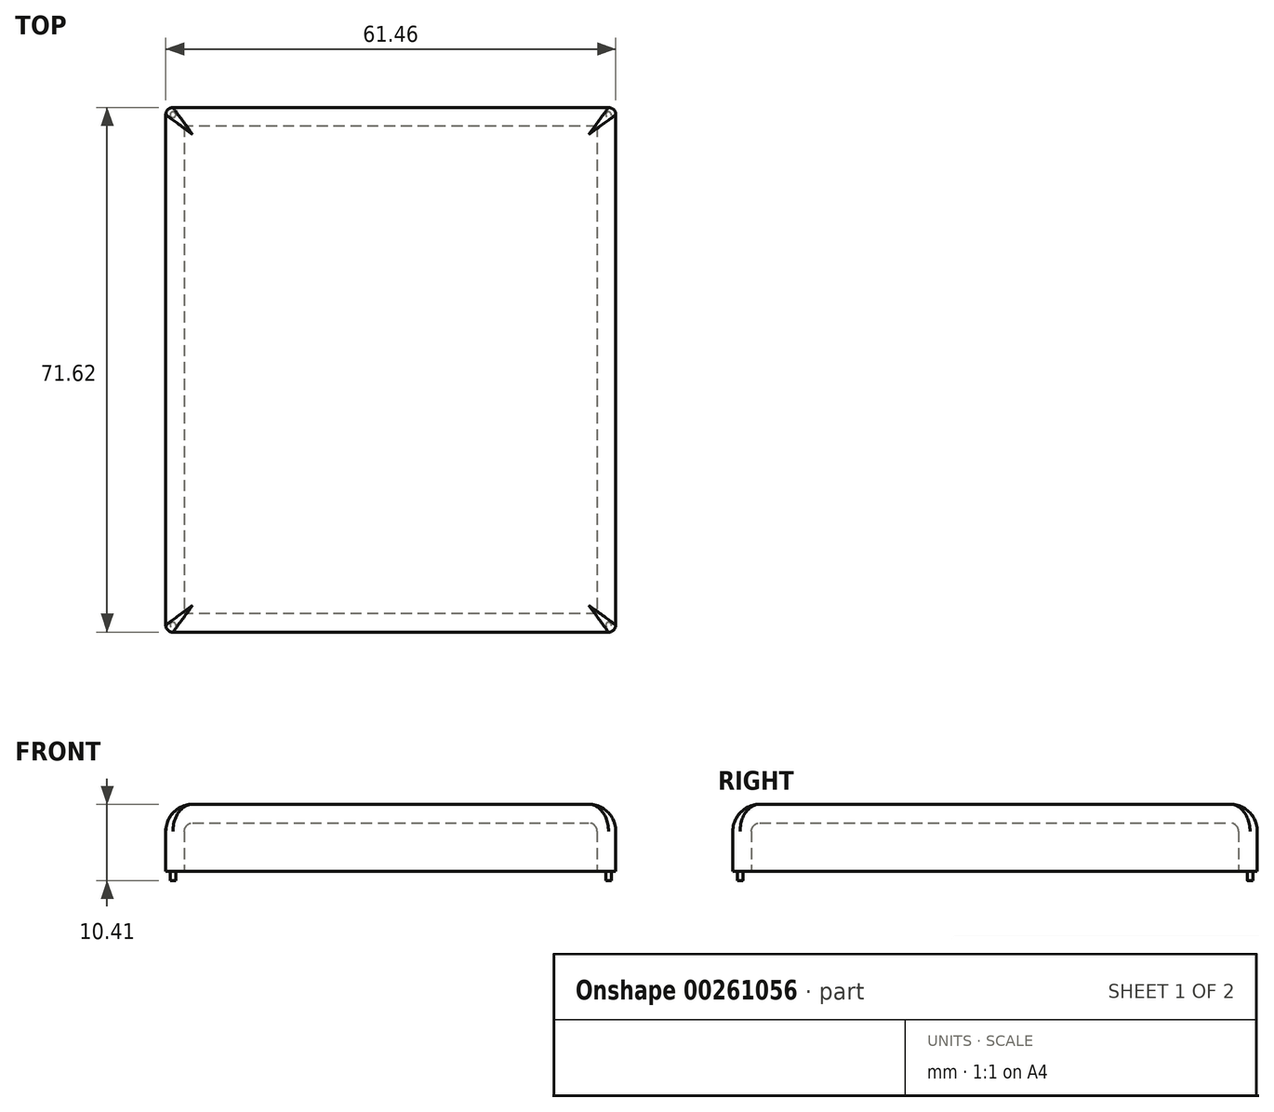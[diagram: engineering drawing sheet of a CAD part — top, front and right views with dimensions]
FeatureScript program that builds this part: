
annotation { "Feature Type Name" : "Feature", "Feature Type Description" : "" }
export const myFeature = defineFeature(function(context is Context, id is Id, definition is map)
    precondition{}
    {
        {
            var Q0;
            Q0=qCreatedBy(makeId("Top.planeOp"),FACE);
            var sketch = newSketch(context, id + "F0", { "sketchPlane" : qUnion([Q0])});
            skLineSegment(sketch, "E0.bottom", {"start": v(30.73, 35.81) * mm, "end": v(-30.73, 35.81) * mm});
            skLineSegment(sketch, "E0.top", {"start": v(30.73, -35.81) * mm, "end": v(-30.73, -35.81) * mm});
            skLineSegment(sketch, "E0.left", {"start": v(30.73, 35.81) * mm, "end": v(30.73, -35.81) * mm});
            skLineSegment(sketch, "E0.right", {"start": v(-30.73, 35.81) * mm, "end": v(-30.73, -35.81) * mm});
            skPoint(sketch, "E0.middle", {"position": v(0, 0) * mm});
            skSolve(sketch);
        }
        {
            var Q0;
            Q0 = qSketchRegion(id + "F0", true);
            extrude(context, id + "F1", {"entities" : qUnion([Q0]), "endBound" : BoundingType.SYMMETRIC, "depth" : 9.14 * mm});
        }
        {
            var Q0;
            Q0=makeQuery(id+"F1.opExtrude","CAP_FACE",FACE,{"disambiguationData":[OSD([sQuery(id+"F0.wireOp",EDGE,"E0.bottom"),sQuery(id+"F0.wireOp",EDGE,"E0.top"),sQuery(id+"F0.wireOp",EDGE,"E0.left"),sQuery(id+"F0.wireOp",EDGE,"E0.right")])],"isStart":false});
            fillet(context, id + "F2", {"entities" : qUnion([Q0]), "radius" : 3.68 * mm, "tangentPropagation" : true, "allowEdgeOverflow" : false});
        }
        {
            var Q0;
            Q0=makeQuery(id+"F1.opExtrude","SWEPT_EDGE",EDGE,{"disambiguationData":[OSD([sQuery(id+"F0.wireOp",EDGE,"E0.top"),sQuery(id+"F0.wireOp",EDGE,"E0.right")])]});
            var Q1;
            Q1=makeQuery(id+"F1.opExtrude","SWEPT_EDGE",EDGE,{"disambiguationData":[OSD([sQuery(id+"F0.wireOp",EDGE,"E0.top"),sQuery(id+"F0.wireOp",EDGE,"E0.left")])]});
            var Q2;
            Q2=makeQuery(id+"F1.opExtrude","SWEPT_EDGE",EDGE,{"disambiguationData":[OSD([sQuery(id+"F0.wireOp",EDGE,"E0.bottom"),sQuery(id+"F0.wireOp",EDGE,"E0.right")])]});
            var Q3;
            Q3=makeQuery(id+"F1.opExtrude","SWEPT_EDGE",EDGE,{"disambiguationData":[OSD([sQuery(id+"F0.wireOp",EDGE,"E0.bottom"),sQuery(id+"F0.wireOp",EDGE,"E0.left")])]});
            fillet(context, id + "F3", {"entities" : qUnion([Q0, Q1, Q2, Q3]), "radius" : 0.98 * mm, "tangentPropagation" : true, "allowEdgeOverflow" : false});
        }
        {
            var Q0;
            Q0=makeQuery(id+"F1.opExtrude","CAP_FACE",FACE,{"disambiguationData":[OSD([sQuery(id+"F0.wireOp",EDGE,"E0.bottom"),sQuery(id+"F0.wireOp",EDGE,"E0.top"),sQuery(id+"F0.wireOp",EDGE,"E0.left"),sQuery(id+"F0.wireOp",EDGE,"E0.right")])],"isStart":true});
            var sketch = newSketch(context, id + "F4", { "sketchPlane" : qUnion([Q0])});
            skLineSegment(sketch, "E1.bottom", {"start": v(26.6, 31.53) * mm, "end": v(-26.6, 31.53) * mm});
            skLineSegment(sketch, "E1.top", {"start": v(26.6, -31.53) * mm, "end": v(-26.6, -31.53) * mm});
            skLineSegment(sketch, "E1.left", {"start": v(26.6, 31.53) * mm, "end": v(26.6, -31.53) * mm});
            skLineSegment(sketch, "E1.right", {"start": v(-26.6, 31.53) * mm, "end": v(-26.6, -31.53) * mm});
            skPoint(sketch, "E1.middle", {"position": v(0, 0) * mm});
            skCircle(sketch, "E2", {"center": v(-29.75, 34.83) * mm, "radius": 0.38 * mm});
            skSolve(sketch);
        }
        {
            var Q0;
            Q0 = qSketchRegion(id + "F4", true);
            extrude(context, id + "F5", {"entities" : qUnion([Q0]), "operationType" : NewBodyOperationType.ADD, "oppositeDirection" : true, "depth" : 4.83 * mm});
        }
        {
            var Q0;
            Q0=makeQuery(id+"F1.opExtrude","CAP_FACE",FACE,{"disambiguationData":[OSD([sQuery(id+"F0.wireOp",EDGE,"E0.bottom"),sQuery(id+"F0.wireOp",EDGE,"E0.top"),sQuery(id+"F0.wireOp",EDGE,"E0.left"),sQuery(id+"F0.wireOp",EDGE,"E0.right")])],"isStart":true});
            shell(context, id + "F6", {"entities" : qUnion([Q0]), "thickness" : 2.54 * mm});
        }
        {
            var Q0;
            Q0=makeQuery(id+"F4.imprint","IMPRINT",FACE,{"disambiguationData":[TD([[makeQuery(id+"F4.imprint","IMPRINT",EDGE,{"derivedFrom":sQuery(id+"F4.wireOp",EDGE,"E2")}),1.0]])]});
            extrude(context, id + "F7", {"entities" : qUnion([Q0]), "operationType" : NewBodyOperationType.ADD, "depth" : 1.27 * mm});
        }
        {
            var Q0;
            Q0=makeQuery(id+"F1.opExtrude","SWEPT_BODY",BODY,{"disambiguationData":[OSD([sQuery(id+"F0.wireOp",EDGE,"E0.bottom"),sQuery(id+"F0.wireOp",EDGE,"E0.top"),sQuery(id+"F0.wireOp",EDGE,"E0.left"),sQuery(id+"F0.wireOp",EDGE,"E0.right")])]});
            var Q1;
            Q1=qCreatedBy(makeId("Right.planeOp"),FACE);
            mirror(context, id + "F8", {"operationType" : NewBodyOperationType.ADD, "entities" : qUnion([Q0]), "mirrorPlane" : qUnion([Q1])});
        }
        {
            var Q0;
            Q0=makeQuery(id+"F1.opExtrude","SWEPT_BODY",BODY,{"disambiguationData":[OSD([sQuery(id+"F0.wireOp",EDGE,"E0.bottom"),sQuery(id+"F0.wireOp",EDGE,"E0.top"),sQuery(id+"F0.wireOp",EDGE,"E0.left"),sQuery(id+"F0.wireOp",EDGE,"E0.right")])]});
            var Q1;
            Q1=qCreatedBy(makeId("Front.planeOp"),FACE);
            mirror(context, id + "F9", {"operationType" : NewBodyOperationType.ADD, "entities" : qUnion([Q0]), "mirrorPlane" : qUnion([Q1])});
        }
    });
